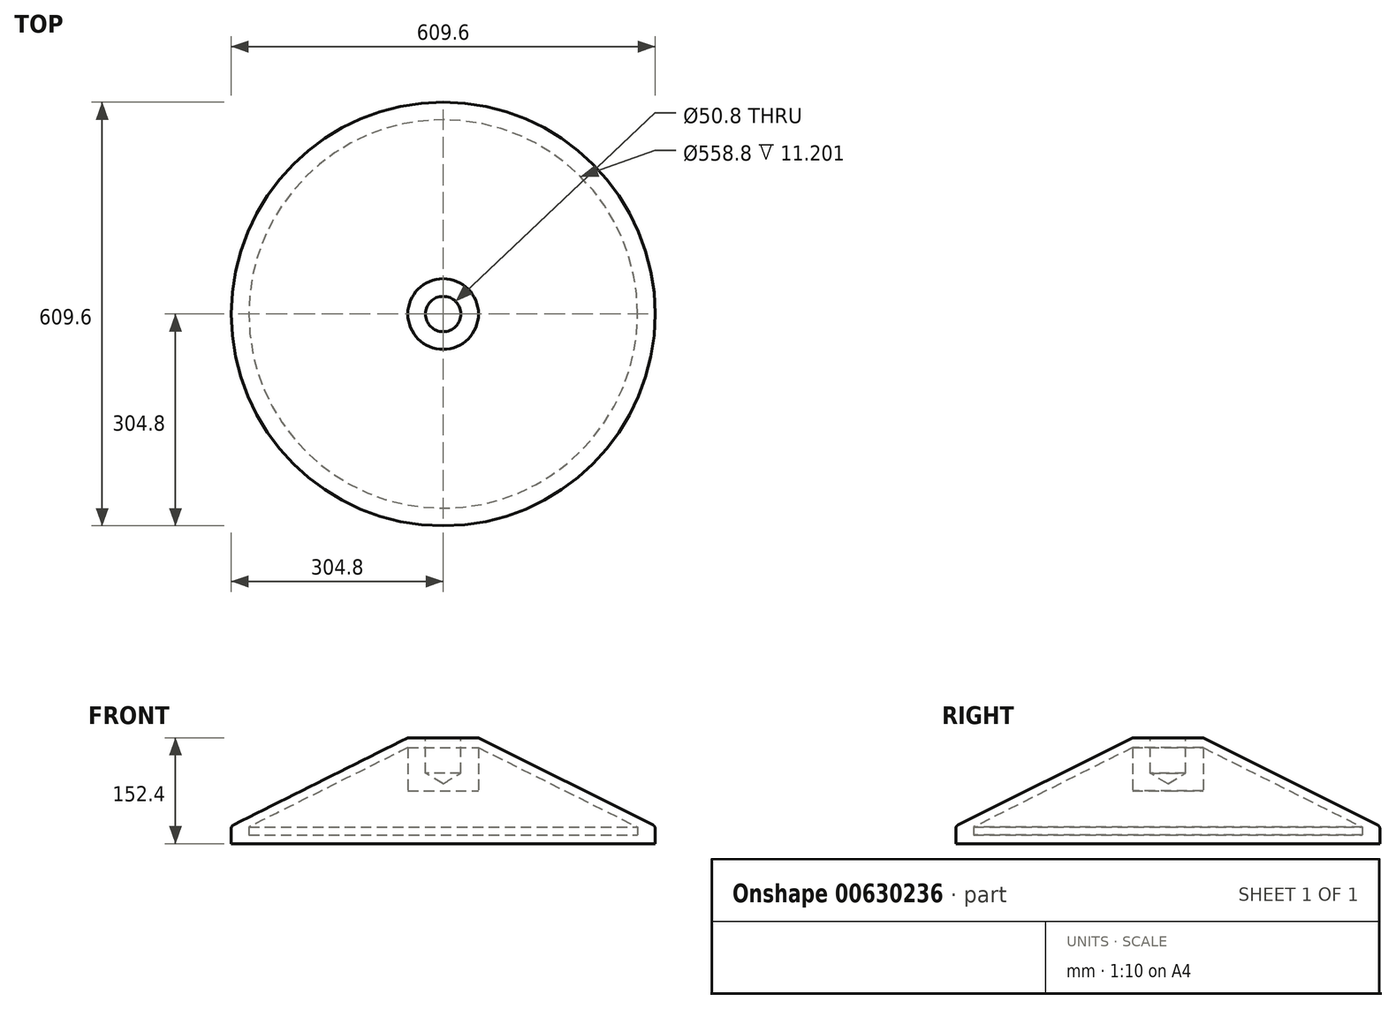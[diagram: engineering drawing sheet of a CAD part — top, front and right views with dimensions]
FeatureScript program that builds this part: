
annotation { "Feature Type Name" : "Feature", "Feature Type Description" : "" }
export const myFeature = defineFeature(function(context is Context, id is Id, definition is map)
    precondition{}
    {
        {
            var Q0;
            Q0=qCreatedBy(makeId("Front.planeOp"),FACE);
            var sketch = newSketch(context, id + "F0", { "sketchPlane" : qUnion([Q0])});
            skLineSegment(sketch, "E0.bottom", {"start": v(0, 0) * mm, "end": v(304.8, 0) * mm});
            skLineSegment(sketch, "E0.top", {"start": v(0, 152.4) * mm, "end": v(50.8, 152.4) * mm});
            skLineSegment(sketch, "E0.left", {"start": v(0, 0) * mm, "end": v(0, 12.7) * mm});
            skLineSegment(sketch, "E0.right", {"start": v(304.8, 0) * mm, "end": v(304.8, 25.4) * mm});
            skLineSegment(sketch, "E1", {"start": v(304.8, 25.4) * mm, "end": v(50.8, 152.4) * mm});
            skLineSegment(sketch, "E2.0", {"start": v(279.4, 12.7) * mm, "end": v(279.4, 23.9) * mm});
            skLineSegment(sketch, "E3.0", {"start": v(279.4, 23.9) * mm, "end": v(50.8, 138.2) * mm});
            skLineSegment(sketch, "E4.0", {"start": v(0, 12.7) * mm, "end": v(279.4, 12.7) * mm});
            skLineSegment(sketch, "E5.0", {"start": v(50.8, 76.2) * mm, "end": v(50.8, 138.2) * mm});
            skLineSegment(sketch, "E6.0", {"start": v(0, 76.2) * mm, "end": v(50.8, 76.2) * mm});
            skLineSegment(sketch, "E7.trimOffspring", {"start": v(0, 76.2) * mm, "end": v(0, 152.4) * mm});
            skSolve(sketch);
        }
        {
            var Q0;
            Q0 = qSketchRegion(id + "F0", true);
            var Q1;
            Q1=sQuery(id+"F0.wireOp",EDGE,"E7.trimOffspring");
            revolve(context, id + "F1", {"entities" : qUnion([Q0]), "axis" : qUnion([Q1]), "revolveType" : RevolveType.FULL});
        }
        {
            var Q0;
            Q0=makeQuery(id+"F1.opRevolve","SWEPT_EDGE",EDGE,{"disambiguationData":[OSD([sQuery(id+"F0.wireOp",EDGE,"E0.right"),sQuery(id+"F0.wireOp",EDGE,"E1")])]});
            fillet(context, id + "F2", {"entities" : qUnion([Q0]), "radius" : 6.35 * mm, "tangentPropagation" : true, "allowEdgeOverflow" : false});
        }
        {
            var Q0;
            Q0=makeQuery(id+"F1.opRevolve","SWEPT_FACE",FACE,{"disambiguationData":[OSD([sQuery(id+"F0.wireOp",EDGE,"E0.top")])]});
            var sketch = newSketch(context, id + "F3", { "sketchPlane" : qUnion([Q0])});
            skPoint(sketch, "E8", {"position": v(0, 0) * mm});
            skSolve(sketch);
        }
        {
            var Q0;
            Q0=sQuery(id+"F3.wireOp",VERTEX,"E8");
            var Q1;
            Q1=makeQuery(id+"F1.opRevolve","SWEPT_BODY",BODY,{"disambiguationData":[OSD([sQuery(id+"F0.wireOp",EDGE,"E0.bottom"),sQuery(id+"F0.wireOp",EDGE,"E0.top"),sQuery(id+"F0.wireOp",EDGE,"E0.left"),sQuery(id+"F0.wireOp",EDGE,"E0.right"),sQuery(id+"F0.wireOp",EDGE,"E1"),sQuery(id+"F0.wireOp",EDGE,"E2.0"),sQuery(id+"F0.wireOp",EDGE,"E3.0"),sQuery(id+"F0.wireOp",EDGE,"E4.0"),sQuery(id+"F0.wireOp",EDGE,"E5.0"),sQuery(id+"F0.wireOp",EDGE,"E6.0"),sQuery(id+"F0.wireOp",EDGE,"E7.trimOffspring")])]});
            hole(context, id + "F4", {"style" : HoleStyle.SIMPLE, "endStyle" : HoleEndStyle.BLIND, "holeDiameter" : 50.8 * mm, "majorDiameter" : 6.35 * mm, "holeDepth" : 50.8 * mm, "isTappedThrough" : true, "tappedDepth" : 12.7 * mm, "tapClearance" : 3, "startFromSketch" : true, "locations" : qUnion([Q0]), "scope" : qUnion([Q1])});
        }
    });
